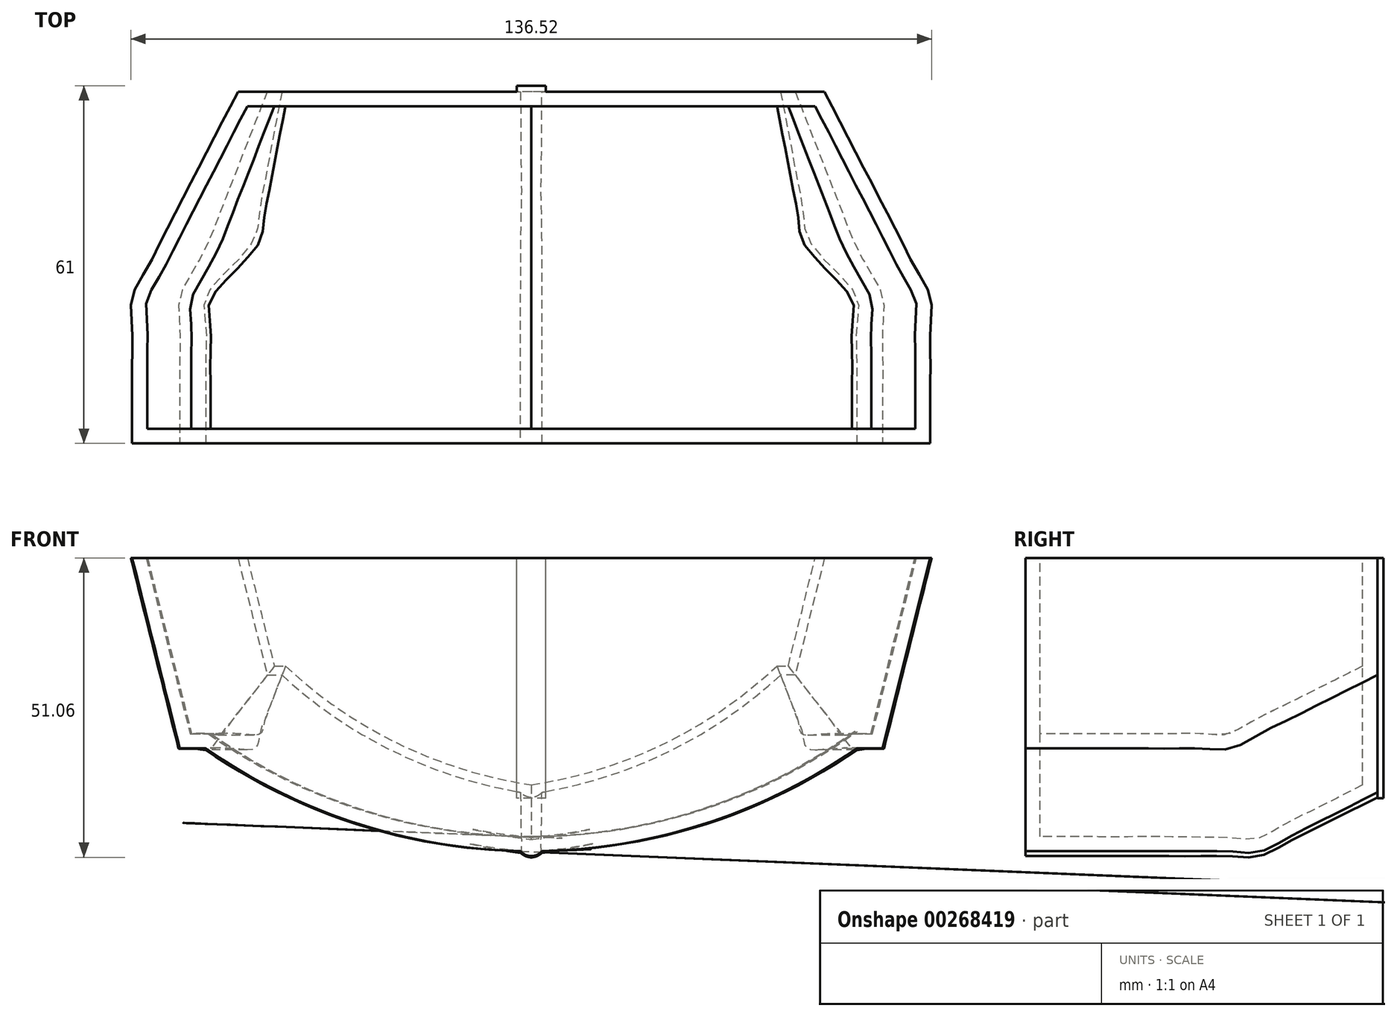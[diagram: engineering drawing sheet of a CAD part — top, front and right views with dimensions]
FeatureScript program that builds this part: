
annotation { "Feature Type Name" : "Feature", "Feature Type Description" : "" }
export const myFeature = defineFeature(function(context is Context, id is Id, definition is map)
    precondition{}
    {
        {
            var Q0;
            Q0=qCreatedBy(makeId("Front.planeOp"),FACE);
            var sketch = newSketch(context, id + "F0", { "sketchPlane" : qUnion([Q0])});
            skLineSegment(sketch, "E0", {"start": v(0, 0) * mm, "end": v(-50, 0) * mm});
            skLineSegment(sketch, "E1", {"start": v(-50, 0) * mm, "end": v(-45, -20) * mm});
            skPoint(sketch, "E2.end.orphan", {"position": v(-50, -20) * mm});
            skPoint(sketch, "E3", {"position": v(-22.57, -30.16) * mm});
            skPoint(sketch, "E4.end.orphan", {"position": v(-23.39, -33.05) * mm});
            skLineSegment(sketch, "E5", {"start": v(-45, -20) * mm, "end": v(-42.5, -20) * mm});
            skPoint(sketch, "E6.end.orphan", {"position": v(0, -40) * mm});
            skArc(sketch, "E7", {"start": v(-42.5, -20) * mm, "mid": v(-23.92, -32.78) * mm, "end": v(-2.5, -39.85) * mm});
            skLineSegment(sketch, "E8", {"start": v(-2.5, -39.85) * mm, "end": v(-2.5, -40.85) * mm});
            skLineSegment(sketch, "E9", {"start": v(-2.5, -40.85) * mm, "end": v(0, -40.85) * mm});
            skPoint(sketch, "E10", {"position": v(-2.5, -39.85) * mm});
            skPoint(sketch, "E11.start.orphan", {"position": v(0, -38.85) * mm});
            skPoint(sketch, "E12.orphan", {"position": v(0.33, -40.3) * mm});
            skPoint(sketch, "E13.orphan", {"position": v(-2.5, -37.35) * mm});
            skPoint(sketch, "E14.MirrorCS.end.orphan", {"position": v(50, 0) * mm});
            skPoint(sketch, "E14.MirrorCS.start.orphan", {"position": v(0, 0) * mm});
            skPoint(sketch, "E15.MirrorCS.end.orphan", {"position": v(45, -20) * mm});
            skPoint(sketch, "E16.MirrorCS.end.orphan", {"position": v(42.5, -20) * mm});
            skPoint(sketch, "E17.MirrorCS.end.orphan", {"position": v(-0.33, -40.3) * mm});
            skLineSegment(sketch, "E18.MirrorCS", {"start": v(50, 0) * mm, "end": v(45, -20) * mm});
            skLineSegment(sketch, "E19.MirrorCS", {"start": v(45, -20) * mm, "end": v(42.5, -20) * mm});
            skLineSegment(sketch, "E20.MirrorCS", {"start": v(0, 0) * mm, "end": v(50, 0) * mm});
            skArc(sketch, "E21.MirrorCS", {"start": v(42.5, -20) * mm, "mid": v(23.92, -32.78) * mm, "end": v(2.5, -39.85) * mm});
            skLineSegment(sketch, "E22.MirrorCS", {"start": v(2.5, -39.85) * mm, "end": v(2.5, -40.85) * mm});
            skLineSegment(sketch, "E23.MirrorCS", {"start": v(2.5, -40.85) * mm, "end": v(0, -40.85) * mm});
            skSolve(sketch);
        }
        {
            var Q0;
            Q0=qCreatedBy(makeId("Front.planeOp"),FACE);
            cPlane(context, id + "F1", {"entities" : qUnion([Q0]), "cplaneType" : CPlaneType.OFFSET, "offset" : 5 * mm, "width" : 150 * mm, "height" : 150 * mm});
        }
        {
            var Q0;
            Q0=qCreatedBy(id+"F1.planeOp",FACE);
            var sketch = newSketch(context, id + "F2", { "sketchPlane" : qUnion([Q0])});
            skLineSegment(sketch, "E24.MirrorCS", {"start": v(0, 0) * mm, "end": v(52.58, 0) * mm});
            skLineSegment(sketch, "E25.1", {"start": v(2.5, -43.35) * mm, "end": v(0, -43.35) * mm});
            skArc(sketch, "E26.0", {"start": v(43.47, -22.5) * mm, "mid": v(24.39, -35.34) * mm, "end": v(2.5, -42.39) * mm});
            skLineSegment(sketch, "E26.1", {"start": v(46.95, -22.5) * mm, "end": v(43.47, -22.5) * mm});
            skLineSegment(sketch, "E26.2", {"start": v(52.58, 0) * mm, "end": v(46.95, -22.5) * mm});
            skLineSegment(sketch, "E27", {"start": v(2.5, -43.35) * mm, "end": v(2.5, -42.39) * mm});
            skPoint(sketch, "E28.start.orphan", {"position": v(0, 0) * mm});
            skLineSegment(sketch, "E29.MirrorCS", {"start": v(0, 0) * mm, "end": v(-52.58, 0) * mm});
            skLineSegment(sketch, "E30.MirrorCS", {"start": v(-52.58, 0) * mm, "end": v(-46.95, -22.5) * mm});
            skLineSegment(sketch, "E31.MirrorCS", {"start": v(-46.95, -22.5) * mm, "end": v(-43.47, -22.5) * mm});
            skArc(sketch, "E32.MirrorCS", {"start": v(-43.47, -22.5) * mm, "mid": v(-24.39, -35.34) * mm, "end": v(-2.5, -42.39) * mm});
            skLineSegment(sketch, "E33.MirrorCS", {"start": v(-2.5, -43.35) * mm, "end": v(-2.5, -42.39) * mm});
            skLineSegment(sketch, "E34.MirrorCS", {"start": v(-2.5, -43.35) * mm, "end": v(0, -43.35) * mm});
            skPoint(sketch, "E35.orphan", {"position": v(-52.58, 0) * mm});
            skSolve(sketch);
        }
        {
            var Q0;
            Q0=qCreatedBy(id+"F1.planeOp",FACE);
            cPlane(context, id + "F3", {"entities" : qUnion([Q0]), "cplaneType" : CPlaneType.OFFSET, "offset" : 5 * mm, "width" : 150 * mm, "height" : 150 * mm});
        }
        {
            var Q0;
            Q0=qCreatedBy(id+"F3.planeOp",FACE);
            var sketch = newSketch(context, id + "F4", { "sketchPlane" : qUnion([Q0])});
            skLineSegment(sketch, "E36.MirrorCS", {"start": v(0, 0) * mm, "end": v(55.15, 0) * mm});
            skPoint(sketch, "E37.start.orphan", {"position": v(0, 0) * mm});
            skArc(sketch, "E38.0", {"start": v(44.42, -25) * mm, "mid": v(24.85, -37.89) * mm, "end": v(2.5, -44.93) * mm});
            skLineSegment(sketch, "E38.1", {"start": v(48.9, -25) * mm, "end": v(44.42, -25) * mm});
            skLineSegment(sketch, "E38.2", {"start": v(55.15, 0) * mm, "end": v(48.9, -25) * mm});
            skLineSegment(sketch, "E39.0", {"start": v(2.5, -45.85) * mm, "end": v(0, -45.85) * mm});
            skLineSegment(sketch, "E40", {"start": v(2.5, -45.85) * mm, "end": v(2.5, -44.93) * mm});
            skLineSegment(sketch, "E41.MirrorCS", {"start": v(0, 0) * mm, "end": v(-55.15, 0) * mm});
            skLineSegment(sketch, "E42.MirrorCS", {"start": v(-55.15, 0) * mm, "end": v(-48.9, -25) * mm});
            skLineSegment(sketch, "E43.MirrorCS", {"start": v(-48.9, -25) * mm, "end": v(-44.42, -25) * mm});
            skArc(sketch, "E44.MirrorCS", {"start": v(-44.42, -25) * mm, "mid": v(-24.85, -37.89) * mm, "end": v(-2.5, -44.93) * mm});
            skLineSegment(sketch, "E45.MirrorCS", {"start": v(-2.5, -45.85) * mm, "end": v(0, -45.85) * mm});
            skLineSegment(sketch, "E46.MirrorCS", {"start": v(-2.5, -45.85) * mm, "end": v(-2.5, -44.93) * mm});
            skSolve(sketch);
        }
        {
            var Q0;
            Q0=qCreatedBy(id+"F3.planeOp",FACE);
            cPlane(context, id + "F5", {"entities" : qUnion([Q0]), "cplaneType" : CPlaneType.OFFSET, "offset" : 5 * mm, "width" : 150 * mm, "height" : 150 * mm});
        }
        {
            var Q0;
            Q0=qCreatedBy(id+"F5.planeOp",FACE);
            var sketch = newSketch(context, id + "F6", { "sketchPlane" : qUnion([Q0])});
            skLineSegment(sketch, "E47.MirrorCS", {"start": v(0, 0) * mm, "end": v(57.73, 0) * mm});
            skPoint(sketch, "E48.start.orphan", {"position": v(0, 0) * mm});
            skArc(sketch, "E49.0", {"start": v(45.35, -27.5) * mm, "mid": v(25.3, -40.44) * mm, "end": v(2.5, -47.46) * mm});
            skLineSegment(sketch, "E49.1", {"start": v(50.86, -27.5) * mm, "end": v(45.35, -27.5) * mm});
            skLineSegment(sketch, "E49.2", {"start": v(57.73, 0) * mm, "end": v(50.86, -27.5) * mm});
            skLineSegment(sketch, "E50.0", {"start": v(2.5, -48.35) * mm, "end": v(0, -48.35) * mm});
            skLineSegment(sketch, "E51", {"start": v(2.5, -48.35) * mm, "end": v(2.5, -47.46) * mm});
            skLineSegment(sketch, "E52.MirrorCS", {"start": v(0, 0) * mm, "end": v(-57.73, 0) * mm});
            skLineSegment(sketch, "E53.MirrorCS", {"start": v(-57.73, 0) * mm, "end": v(-50.86, -27.5) * mm});
            skLineSegment(sketch, "E54.MirrorCS", {"start": v(-50.86, -27.5) * mm, "end": v(-45.35, -27.5) * mm});
            skArc(sketch, "E55.MirrorCS", {"start": v(-45.35, -27.5) * mm, "mid": v(-25.3, -40.44) * mm, "end": v(-2.5, -47.46) * mm});
            skLineSegment(sketch, "E56.MirrorCS", {"start": v(-2.5, -48.35) * mm, "end": v(-2.5, -47.46) * mm});
            skLineSegment(sketch, "E57.MirrorCS", {"start": v(-2.5, -48.35) * mm, "end": v(0, -48.35) * mm});
            skSolve(sketch);
        }
        {
            var Q0;
            Q0=qCreatedBy(id+"F5.planeOp",FACE);
            cPlane(context, id + "F7", {"entities" : qUnion([Q0]), "cplaneType" : CPlaneType.OFFSET, "offset" : 5 * mm, "width" : 150 * mm, "height" : 150 * mm});
        }
        {
            var Q0;
            Q0=qCreatedBy(id+"F7.planeOp",FACE);
            var sketch = newSketch(context, id + "F8", { "sketchPlane" : qUnion([Q0])});
            skLineSegment(sketch, "E58.MirrorCS", {"start": v(0, 0) * mm, "end": v(60.3, 0) * mm});
            skPoint(sketch, "E59.start.orphan", {"position": v(0, 0) * mm});
            skArc(sketch, "E60.0", {"start": v(46.27, -30) * mm, "mid": v(25.75, -42.99) * mm, "end": v(2.5, -50) * mm});
            skLineSegment(sketch, "E60.1", {"start": v(52.8, -30) * mm, "end": v(46.27, -30) * mm});
            skLineSegment(sketch, "E60.2", {"start": v(60.3, 0) * mm, "end": v(52.8, -30) * mm});
            skLineSegment(sketch, "E61.0", {"start": v(2.5, -50.85) * mm, "end": v(0, -50.85) * mm});
            skLineSegment(sketch, "E62", {"start": v(2.5, -50.85) * mm, "end": v(2.5, -50) * mm});
            skLineSegment(sketch, "E63.MirrorCS", {"start": v(-2.5, -50.85) * mm, "end": v(-2.5, -50) * mm});
            skLineSegment(sketch, "E64.MirrorCS", {"start": v(-2.5, -50.85) * mm, "end": v(0, -50.85) * mm});
            skLineSegment(sketch, "E65.MirrorCS", {"start": v(0, 0) * mm, "end": v(-60.3, 0) * mm});
            skArc(sketch, "E66.MirrorCS", {"start": v(-46.27, -30) * mm, "mid": v(-25.75, -42.99) * mm, "end": v(-2.5, -50) * mm});
            skLineSegment(sketch, "E67.MirrorCS", {"start": v(-60.3, 0) * mm, "end": v(-52.8, -30) * mm});
            skLineSegment(sketch, "E68.MirrorCS", {"start": v(-52.8, -30) * mm, "end": v(-46.27, -30) * mm});
            skSolve(sketch);
        }
        {
            var Q0;
            Q0=qCreatedBy(makeId("Front.planeOp"),FACE);
            cPlane(context, id + "F9", {"entities" : qUnion([Q0]), "cplaneType" : CPlaneType.OFFSET, "offset" : 25 * mm, "width" : 150 * mm, "height" : 150 * mm});
        }
        {
            var Q0;
            Q0=qCreatedBy(id+"F9.planeOp",FACE);
            var sketch = newSketch(context, id + "F10", { "sketchPlane" : qUnion([Q0])});
            skLineSegment(sketch, "E69.MirrorCS", {"start": v(0, 0) * mm, "end": v(62.88, 0) * mm});
            skLineSegment(sketch, "E70.0", {"start": v(2.5, -50.85) * mm, "end": v(0, -50.85) * mm});
            skLineSegment(sketch, "E71", {"start": v(2.5, -50.85) * mm, "end": v(2.5, -50) * mm});
            skArc(sketch, "E72.0", {"start": v(47.18, -32.5) * mm, "mid": v(26, -44.2) * mm, "end": v(2.5, -50) * mm});
            skLineSegment(sketch, "E72.1", {"start": v(54.76, -32.5) * mm, "end": v(47.18, -32.5) * mm});
            skLineSegment(sketch, "E72.2", {"start": v(62.88, 0) * mm, "end": v(54.76, -32.5) * mm});
            skLineSegment(sketch, "E73.MirrorCS", {"start": v(-2.5, -50.85) * mm, "end": v(-2.5, -50) * mm});
            skLineSegment(sketch, "E74.MirrorCS", {"start": v(-2.5, -50.85) * mm, "end": v(0, -50.85) * mm});
            skArc(sketch, "E75.MirrorCS", {"start": v(-47.18, -32.5) * mm, "mid": v(-26, -44.2) * mm, "end": v(-2.5, -50) * mm});
            skLineSegment(sketch, "E76.MirrorCS", {"start": v(0, 0) * mm, "end": v(-62.88, 0) * mm});
            skLineSegment(sketch, "E77.MirrorCS", {"start": v(-54.76, -32.5) * mm, "end": v(-47.18, -32.5) * mm});
            skLineSegment(sketch, "E78.MirrorCS", {"start": v(-62.88, 0) * mm, "end": v(-54.76, -32.5) * mm});
            skSolve(sketch);
        }
        {
            var Q0;
            Q0=qCreatedBy(id+"F9.planeOp",FACE);
            cPlane(context, id + "F11", {"entities" : qUnion([Q0]), "cplaneType" : CPlaneType.OFFSET, "offset" : 5 * mm, "width" : 150 * mm, "height" : 150 * mm});
        }
        {
            var Q0;
            Q0=qCreatedBy(id+"F11.planeOp",FACE);
            var sketch = newSketch(context, id + "F12", { "sketchPlane" : qUnion([Q0])});
            skLineSegment(sketch, "E79.MirrorCS", {"start": v(0, 0) * mm, "end": v(65.46, 0) * mm});
            skLineSegment(sketch, "E80.0", {"start": v(2.5, -50.85) * mm, "end": v(0, -50.85) * mm});
            skLineSegment(sketch, "E81", {"start": v(2.5, -50.85) * mm, "end": v(2.5, -50) * mm});
            skLineSegment(sketch, "E82.1", {"start": v(57.34, -32.5) * mm, "end": v(51.29, -32.5) * mm});
            skLineSegment(sketch, "E83.0", {"start": v(65.46, 0) * mm, "end": v(57.34, -32.5) * mm});
            skArc(sketch, "E84.0", {"start": v(51.29, -32.5) * mm, "mid": v(28.11, -44.65) * mm, "end": v(2.5, -50) * mm});
            skLineSegment(sketch, "E85.MirrorCS", {"start": v(-2.5, -50.85) * mm, "end": v(-2.5, -50) * mm});
            skLineSegment(sketch, "E86.MirrorCS", {"start": v(-2.5, -50.85) * mm, "end": v(0, -50.85) * mm});
            skLineSegment(sketch, "E87.MirrorCS", {"start": v(-57.34, -32.5) * mm, "end": v(-51.29, -32.5) * mm});
            skArc(sketch, "E88.MirrorCS", {"start": v(-51.29, -32.5) * mm, "mid": v(-28.11, -44.65) * mm, "end": v(-2.5, -50) * mm});
            skLineSegment(sketch, "E89.MirrorCS", {"start": v(-65.46, 0) * mm, "end": v(-57.34, -32.5) * mm});
            skLineSegment(sketch, "E90.MirrorCS", {"start": v(0, 0) * mm, "end": v(-65.46, 0) * mm});
            skSolve(sketch);
        }
        {
            var Q0;
            Q0=qCreatedBy(id+"F11.planeOp",FACE);
            cPlane(context, id + "F13", {"entities" : qUnion([Q0]), "cplaneType" : CPlaneType.OFFSET, "offset" : 5 * mm, "width" : 150 * mm, "height" : 150 * mm});
        }
        {
            var Q0;
            Q0=qCreatedBy(id+"F13.planeOp",FACE);
            var sketch = newSketch(context, id + "F14", { "sketchPlane" : qUnion([Q0])});
            skLineSegment(sketch, "E91.MirrorCS", {"start": v(0, 0) * mm, "end": v(68.04, 0) * mm});
            skLineSegment(sketch, "E92.0", {"start": v(2.5, -50.85) * mm, "end": v(0, -50.85) * mm});
            skLineSegment(sketch, "E93", {"start": v(2.5, -50.85) * mm, "end": v(2.5, -50) * mm});
            skLineSegment(sketch, "E94.1", {"start": v(59.91, -32.5) * mm, "end": v(55.48, -32.5) * mm});
            skLineSegment(sketch, "E95.0", {"start": v(68.04, 0) * mm, "end": v(59.91, -32.5) * mm});
            skArc(sketch, "E96.0", {"start": v(55.48, -32.5) * mm, "mid": v(30.27, -45.13) * mm, "end": v(2.5, -50) * mm});
            skLineSegment(sketch, "E97.MirrorCS", {"start": v(-2.5, -50.85) * mm, "end": v(-2.5, -50) * mm});
            skLineSegment(sketch, "E98.MirrorCS", {"start": v(-2.5, -50.85) * mm, "end": v(0, -50.85) * mm});
            skLineSegment(sketch, "E99.MirrorCS", {"start": v(-59.91, -32.5) * mm, "end": v(-55.48, -32.5) * mm});
            skLineSegment(sketch, "E100.MirrorCS", {"start": v(0, 0) * mm, "end": v(-68.04, 0) * mm});
            skLineSegment(sketch, "E101.MirrorCS", {"start": v(-68.04, 0) * mm, "end": v(-59.91, -32.5) * mm});
            skArc(sketch, "E102.MirrorCS", {"start": v(-55.48, -32.5) * mm, "mid": v(-30.27, -45.13) * mm, "end": v(-2.5, -50) * mm});
            skSolve(sketch);
        }
        {
            var Q0;
            Q0=qCreatedBy(id+"F13.planeOp",FACE);
            cPlane(context, id + "F15", {"entities" : qUnion([Q0]), "cplaneType" : CPlaneType.OFFSET, "offset" : 5 * mm, "width" : 150 * mm, "height" : 150 * mm});
        }
        {
            var Q0;
            Q0=qCreatedBy(id+"F15.planeOp",FACE);
            var sketch = newSketch(context, id + "F16", { "sketchPlane" : qUnion([Q0])});
            skLineSegment(sketch, "E103.MirrorCS", {"start": v(0, 0) * mm, "end": v(68.04, 0) * mm});
            skLineSegment(sketch, "E104.0", {"start": v(2.5, -50.85) * mm, "end": v(0, -50.85) * mm});
            skLineSegment(sketch, "E105", {"start": v(2.5, -50.85) * mm, "end": v(2.5, -50) * mm});
            skLineSegment(sketch, "E106.1", {"start": v(59.91, -32.5) * mm, "end": v(55.48, -32.5) * mm});
            skLineSegment(sketch, "E107.0", {"start": v(68.04, 0) * mm, "end": v(59.91, -32.5) * mm});
            skArc(sketch, "E108.0", {"start": v(55.48, -32.5) * mm, "mid": v(30.27, -45.13) * mm, "end": v(2.5, -50) * mm});
            skLineSegment(sketch, "E109.MirrorCS", {"start": v(-2.5, -50.85) * mm, "end": v(-2.5, -50) * mm});
            skLineSegment(sketch, "E110.MirrorCS", {"start": v(-2.5, -50.85) * mm, "end": v(0, -50.85) * mm});
            skLineSegment(sketch, "E111.MirrorCS", {"start": v(-59.91, -32.5) * mm, "end": v(-55.48, -32.5) * mm});
            skLineSegment(sketch, "E112.MirrorCS", {"start": v(0, 0) * mm, "end": v(-68.04, 0) * mm});
            skLineSegment(sketch, "E113.MirrorCS", {"start": v(-68.04, 0) * mm, "end": v(-59.91, -32.5) * mm});
            skArc(sketch, "E114.MirrorCS", {"start": v(-55.48, -32.5) * mm, "mid": v(-30.27, -45.13) * mm, "end": v(-2.5, -50) * mm});
            skSolve(sketch);
        }
        {
            var Q0;
            Q0=qCreatedBy(id+"F15.planeOp",FACE);
            cPlane(context, id + "F17", {"entities" : qUnion([Q0]), "cplaneType" : CPlaneType.OFFSET, "offset" : 5 * mm, "width" : 150 * mm, "height" : 150 * mm});
        }
        {
            var Q0;
            Q0=qCreatedBy(id+"F17.planeOp",FACE);
            var sketch = newSketch(context, id + "F18", { "sketchPlane" : qUnion([Q0])});
            skLineSegment(sketch, "E115.MirrorCS", {"start": v(0, 0) * mm, "end": v(68.04, 0) * mm});
            skLineSegment(sketch, "E116.0", {"start": v(2.5, -50.85) * mm, "end": v(0, -50.85) * mm});
            skLineSegment(sketch, "E117", {"start": v(2.5, -50.85) * mm, "end": v(2.5, -50) * mm});
            skLineSegment(sketch, "E118.1", {"start": v(59.91, -32.5) * mm, "end": v(55.48, -32.5) * mm});
            skLineSegment(sketch, "E119.0", {"start": v(68.04, 0) * mm, "end": v(59.91, -32.5) * mm});
            skArc(sketch, "E120.0", {"start": v(55.48, -32.5) * mm, "mid": v(30.27, -45.13) * mm, "end": v(2.5, -50) * mm});
            skLineSegment(sketch, "E121.MirrorCS", {"start": v(-2.5, -50.85) * mm, "end": v(-2.5, -50) * mm});
            skLineSegment(sketch, "E122.MirrorCS", {"start": v(-2.5, -50.85) * mm, "end": v(0, -50.85) * mm});
            skLineSegment(sketch, "E123.MirrorCS", {"start": v(-59.91, -32.5) * mm, "end": v(-55.48, -32.5) * mm});
            skLineSegment(sketch, "E124.MirrorCS", {"start": v(0, 0) * mm, "end": v(-68.04, 0) * mm});
            skLineSegment(sketch, "E125.MirrorCS", {"start": v(-68.04, 0) * mm, "end": v(-59.91, -32.5) * mm});
            skArc(sketch, "E126.MirrorCS", {"start": v(-55.48, -32.5) * mm, "mid": v(-30.27, -45.13) * mm, "end": v(-2.5, -50) * mm});
            skSolve(sketch);
        }
        {
            var Q0;
            Q0=qCreatedBy(id+"F17.planeOp",FACE);
            cPlane(context, id + "F19", {"entities" : qUnion([Q0]), "cplaneType" : CPlaneType.OFFSET, "offset" : 5 * mm, "width" : 150 * mm, "height" : 150 * mm});
        }
        {
            var Q0;
            Q0=qCreatedBy(id+"F19.planeOp",FACE);
            var sketch = newSketch(context, id + "F20", { "sketchPlane" : qUnion([Q0])});
            skLineSegment(sketch, "E127.MirrorCS", {"start": v(0, 0) * mm, "end": v(68.04, 0) * mm});
            skLineSegment(sketch, "E128.0", {"start": v(2.5, -50.85) * mm, "end": v(0, -50.85) * mm});
            skLineSegment(sketch, "E129", {"start": v(2.5, -50.85) * mm, "end": v(2.5, -50) * mm});
            skLineSegment(sketch, "E130.1", {"start": v(59.91, -32.5) * mm, "end": v(55.48, -32.5) * mm});
            skLineSegment(sketch, "E131.0", {"start": v(68.04, 0) * mm, "end": v(59.91, -32.5) * mm});
            skArc(sketch, "E132.0", {"start": v(55.48, -32.5) * mm, "mid": v(30.27, -45.13) * mm, "end": v(2.5, -50) * mm});
            skLineSegment(sketch, "E133.MirrorCS", {"start": v(-2.5, -50.85) * mm, "end": v(-2.5, -50) * mm});
            skLineSegment(sketch, "E134.MirrorCS", {"start": v(-2.5, -50.85) * mm, "end": v(0, -50.85) * mm});
            skLineSegment(sketch, "E135.MirrorCS", {"start": v(-59.91, -32.5) * mm, "end": v(-55.48, -32.5) * mm});
            skLineSegment(sketch, "E136.MirrorCS", {"start": v(0, 0) * mm, "end": v(-68.04, 0) * mm});
            skLineSegment(sketch, "E137.MirrorCS", {"start": v(-68.04, 0) * mm, "end": v(-59.91, -32.5) * mm});
            skArc(sketch, "E138.MirrorCS", {"start": v(-55.48, -32.5) * mm, "mid": v(-30.27, -45.13) * mm, "end": v(-2.5, -50) * mm});
            skSolve(sketch);
        }
        {
            var Q0;
            Q0=qCreatedBy(id+"F19.planeOp",FACE);
            cPlane(context, id + "F21", {"entities" : qUnion([Q0]), "cplaneType" : CPlaneType.OFFSET, "offset" : 5 * mm, "width" : 150 * mm, "height" : 150 * mm});
        }
        {
            var Q0;
            Q0=qCreatedBy(id+"F21.planeOp",FACE);
            var sketch = newSketch(context, id + "F22", { "sketchPlane" : qUnion([Q0])});
            skLineSegment(sketch, "E139.MirrorCS", {"start": v(0, 0) * mm, "end": v(68.04, 0) * mm});
            skLineSegment(sketch, "E140.0", {"start": v(2.5, -50.85) * mm, "end": v(0, -50.85) * mm});
            skLineSegment(sketch, "E141", {"start": v(2.5, -50.85) * mm, "end": v(2.5, -50) * mm});
            skLineSegment(sketch, "E142.1", {"start": v(59.91, -32.5) * mm, "end": v(55.48, -32.5) * mm});
            skLineSegment(sketch, "E143.0", {"start": v(68.04, 0) * mm, "end": v(59.91, -32.5) * mm});
            skArc(sketch, "E144.0", {"start": v(55.48, -32.5) * mm, "mid": v(30.27, -45.13) * mm, "end": v(2.5, -50) * mm});
            skLineSegment(sketch, "E145.MirrorCS", {"start": v(-2.5, -50.85) * mm, "end": v(-2.5, -50) * mm});
            skLineSegment(sketch, "E146.MirrorCS", {"start": v(-2.5, -50.85) * mm, "end": v(0, -50.85) * mm});
            skLineSegment(sketch, "E147.MirrorCS", {"start": v(-59.91, -32.5) * mm, "end": v(-55.48, -32.5) * mm});
            skLineSegment(sketch, "E148.MirrorCS", {"start": v(0, 0) * mm, "end": v(-68.04, 0) * mm});
            skLineSegment(sketch, "E149.MirrorCS", {"start": v(-68.04, 0) * mm, "end": v(-59.91, -32.5) * mm});
            skArc(sketch, "E150.MirrorCS", {"start": v(-55.48, -32.5) * mm, "mid": v(-30.27, -45.13) * mm, "end": v(-2.5, -50) * mm});
            skSolve(sketch);
        }
        {
            var Q0;
            Q0=qCreatedBy(id+"F21.planeOp",FACE);
            cPlane(context, id + "F23", {"entities" : qUnion([Q0]), "cplaneType" : CPlaneType.OFFSET, "offset" : 5 * mm, "width" : 150 * mm, "height" : 150 * mm});
        }
        {
            var Q0;
            Q0=qCreatedBy(id+"F23.planeOp",FACE);
            var sketch = newSketch(context, id + "F24", { "sketchPlane" : qUnion([Q0])});
            skLineSegment(sketch, "E151.MirrorCS", {"start": v(0, 0) * mm, "end": v(68.04, 0) * mm});
            skLineSegment(sketch, "E152.0", {"start": v(2.5, -50.85) * mm, "end": v(0, -50.85) * mm});
            skLineSegment(sketch, "E153", {"start": v(2.5, -50.85) * mm, "end": v(2.5, -50) * mm});
            skLineSegment(sketch, "E154.1", {"start": v(59.91, -32.5) * mm, "end": v(55.48, -32.5) * mm});
            skLineSegment(sketch, "E155.0", {"start": v(68.04, 0) * mm, "end": v(59.91, -32.5) * mm});
            skArc(sketch, "E156.0", {"start": v(55.48, -32.5) * mm, "mid": v(30.27, -45.13) * mm, "end": v(2.5, -50) * mm});
            skLineSegment(sketch, "E157.MirrorCS", {"start": v(-2.5, -50.85) * mm, "end": v(-2.5, -50) * mm});
            skLineSegment(sketch, "E158.MirrorCS", {"start": v(-2.5, -50.85) * mm, "end": v(0, -50.85) * mm});
            skLineSegment(sketch, "E159.MirrorCS", {"start": v(-59.91, -32.5) * mm, "end": v(-55.48, -32.5) * mm});
            skLineSegment(sketch, "E160.MirrorCS", {"start": v(0, 0) * mm, "end": v(-68.04, 0) * mm});
            skLineSegment(sketch, "E161.MirrorCS", {"start": v(-68.04, 0) * mm, "end": v(-59.91, -32.5) * mm});
            skArc(sketch, "E162.MirrorCS", {"start": v(-55.48, -32.5) * mm, "mid": v(-30.27, -45.13) * mm, "end": v(-2.5, -50) * mm});
            skSolve(sketch);
        }
        {
            var Q0;
            Q0 = qSketchRegion(id + "F0", true);
            var Q1;
            Q1 = qSketchRegion(id + "F2", true);
            var Q2;
            Q2 = qSketchRegion(id + "F4", true);
            var Q3;
            Q3 = qSketchRegion(id + "F6", true);
            var Q4;
            Q4 = qSketchRegion(id + "F8", true);
            var Q5;
            Q5 = qSketchRegion(id + "F10", true);
            var Q6;
            Q6 = qSketchRegion(id + "F12", true);
            var Q7;
            Q7 = qSketchRegion(id + "F14", true);
            var Q8;
            Q8 = qSketchRegion(id + "F16", true);
            var Q9;
            Q9 = qSketchRegion(id + "F18", true);
            var Q10;
            Q10 = qSketchRegion(id + "F20", true);
            var Q11;
            Q11 = qSketchRegion(id + "F22", true);
            var Q12;
            Q12 = qSketchRegion(id + "F24", true);
            loft(context, id + "F25", {"sheetProfilesArray" : [{ "sheetProfileEntities" : qUnion([Q0]) }, { "sheetProfileEntities" : qUnion([Q1]) }, { "sheetProfileEntities" : qUnion([Q2]) }, { "sheetProfileEntities" : qUnion([Q3]) }, { "sheetProfileEntities" : qUnion([Q4]) }, { "sheetProfileEntities" : qUnion([Q5]) }, { "sheetProfileEntities" : qUnion([Q6]) }, { "sheetProfileEntities" : qUnion([Q7]) }, { "sheetProfileEntities" : qUnion([Q8]) }, { "sheetProfileEntities" : qUnion([Q9]) }, { "sheetProfileEntities" : qUnion([Q10]) }, { "sheetProfileEntities" : qUnion([Q11]) }, { "sheetProfileEntities" : qUnion([Q12]) }]});
        }
        {
            var Q0;
            Q0=makeQuery(id+"F25.opLoft","SWEPT_FACE",FACE,{"disambiguationData":[OSD([sQuery(id+"F0.wireOp",EDGE,"E0"),sQuery(id+"F0.wireOp",EDGE,"E18.MirrorCS"),sQuery(id+"F0.wireOp",EDGE,"E20.MirrorCS"),sQuery(id+"F2.wireOp",EDGE,"E24.MirrorCS"),sQuery(id+"F2.wireOp",EDGE,"E26.2"),sQuery(id+"F2.wireOp",EDGE,"E29.MirrorCS")])]});
            shell(context, id + "F26", {"entities" : qUnion([Q0]), "thickness" : 2.5 * mm});
        }
        {
            var Q0;
            Q0=qCreatedBy(makeId("Front.planeOp"),FACE);
            var sketch = newSketch(context, id + "F27", { "sketchPlane" : qUnion([Q0])});
            skLineSegment(sketch, "E163", {"start": v(0, -41) * mm, "end": v(2.5, -41) * mm});
            skLineSegment(sketch, "E164.MirrorCS", {"start": v(0, -41) * mm, "end": v(-2.5, -41) * mm});
            skLineSegment(sketch, "E165", {"start": v(-2.5, -41) * mm, "end": v(-2.5, 0) * mm});
            skLineSegment(sketch, "E166", {"start": v(2.5, -41) * mm, "end": v(2.5, 0) * mm});
            skLineSegment(sketch, "E167", {"start": v(2.5, 0) * mm, "end": v(-2.5, 0) * mm});
            skSolve(sketch);
        }
        {
            var Q0;
            Q0 = qSketchRegion(id + "F27", true);
            extrude(context, id + "F28", {"entities" : qUnion([Q0]), "operationType" : NewBodyOperationType.ADD, "depth" : 0 * mm, "hasSecondDirection" : true, "secondDirectionOppositeDirection" : true, "secondDirectionDepth" : 1 * mm});
        }
        {
            var Q0;
            Q0=makeQuery(id+"F25.opLoft","SWEPT_EDGE",EDGE,{"disambiguationData":[OSD([sQuery(id+"F0.wireOp",EDGE,"E8"),sQuery(id+"F0.wireOp",EDGE,"E9"),sQuery(id+"F2.wireOp",EDGE,"E33.MirrorCS"),sQuery(id+"F2.wireOp",EDGE,"E34.MirrorCS")])]});
            var Q1;
            Q1=makeQuery(id+"F25.opLoft","SWEPT_EDGE",EDGE,{"disambiguationData":[OSD([sQuery(id+"F0.wireOp",EDGE,"E22.MirrorCS"),sQuery(id+"F0.wireOp",EDGE,"E23.MirrorCS"),sQuery(id+"F2.wireOp",EDGE,"E25.1"),sQuery(id+"F2.wireOp",EDGE,"E27")])]});
            fillet(context, id + "F29", {"entities" : qUnion([Q0, Q1]), "radius" : 2.5 * mm, "tangentPropagation" : true, "allowEdgeOverflow" : false});
        }
    });
